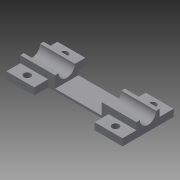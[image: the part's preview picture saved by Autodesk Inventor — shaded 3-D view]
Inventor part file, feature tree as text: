
AUTODESK INVENTOR PART (.ipt)
format: ipt  version: 2013 SP2 (Build 170200200, 200)  size: 131,584 bytes
history: native  units: mm
features: extrude x4, sketch x4
ambient origin geometry x8: Origin, YZ Plane, XZ Plane, XY Plane, X Axis, Y Axis, Z Axis, Center Point
bodies: Solid1 (feature_tree)
feature tree (8):
  extrude  "Extrusion1"  Depth=10.0mm
  extrude  "Extrusion2"  Depth=7.0mm
  extrude  "Extrusion3"  Depth=12.0mm
  extrude  "Extrusion4"  Depth=12.0mm
  sketch  "Sketch1"  dims[d0=50.0mm d1=10.0mm]
  sketch  "Sketch2"  dims[d2=6.0mm d3=0.0mm d4=7.0mm]
  sketch  "Sketch3"  dims[d5=10.0mm d6=0.0mm d15=12.0mm]
  sketch  "Sketch4"  dims[d16=6.0mm d17=12.0mm d18=6.0mm d19=12.0mm d20=6.0mm d21=12.0mm d22=6.0mm d23=3.0mm d24=3.0mm d25=3.0mm d26=3.0mm d27=3.0mm d28=0.0mm d29=20.0mm d31=5.0mm d32=0.0mm]
